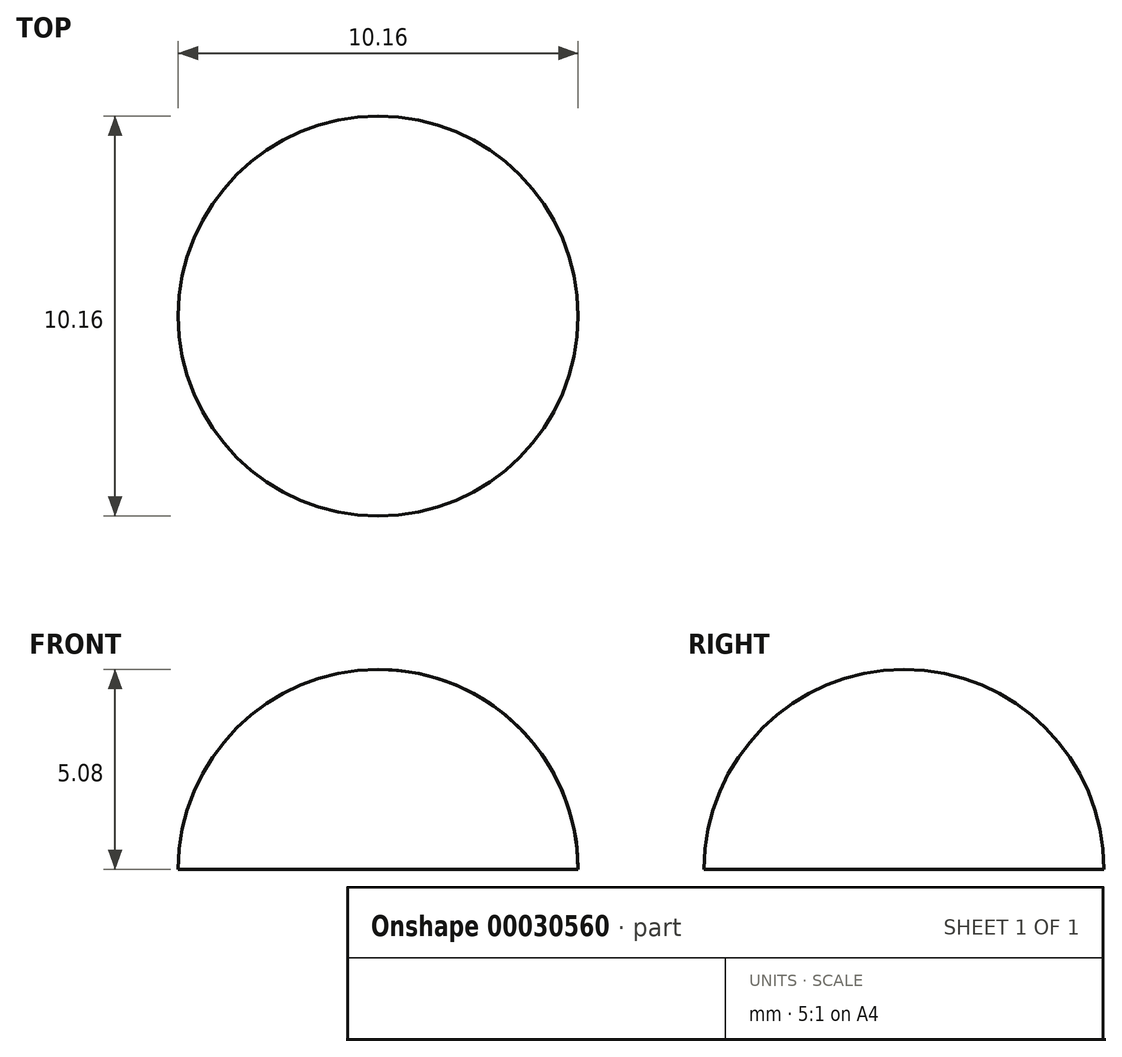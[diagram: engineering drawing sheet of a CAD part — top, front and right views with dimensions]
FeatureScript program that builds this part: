
annotation { "Feature Type Name" : "Feature", "Feature Type Description" : "" }
export const myFeature = defineFeature(function(context is Context, id is Id, definition is map)
    precondition{}
    {
        {
            var Q0;
            Q0=qCreatedBy(makeId("Front.planeOp"),FACE);
            var sketch = newSketch(context, id + "F0", { "sketchPlane" : qUnion([Q0])});
            skLineSegment(sketch, "E0", {"start": v(0, 14.8) * mm, "end": v(0, -14.58) * mm, "construction": true});
            skArc(sketch, "E1", {"start": v(5.08, 0) * mm, "mid": v(3.6, 3.6) * mm, "end": v(0, 5.08) * mm});
            skLineSegment(sketch, "E2", {"start": v(-7.44, 0) * mm, "end": v(7.9, 0) * mm});
            skLineSegment(sketch, "E3", {"start": v(0, 5.08) * mm, "end": v(0, 0) * mm});
            skLineSegment(sketch, "E4", {"start": v(5.08, 0) * mm, "end": v(0, 0) * mm});
            skSolve(sketch);
        }
        {
            var Q0;
            Q0=makeQuery(id+"F0.imprint","IMPRINT",FACE,{"disambiguationData":[TD([[makeQuery(id+"F0.imprint","IMPRINT",EDGE,{"derivedFrom":sQuery(id+"F0.wireOp",EDGE,"E1")}),1.0]])]});
            var Q1;
            Q1=sQuery(id+"F0.wireOp",EDGE,"E0");
            revolve(context, id + "F1", {"entities" : qUnion([Q0]), "axis" : qUnion([Q1]), "revolveType" : RevolveType.FULL});
        }
    });
